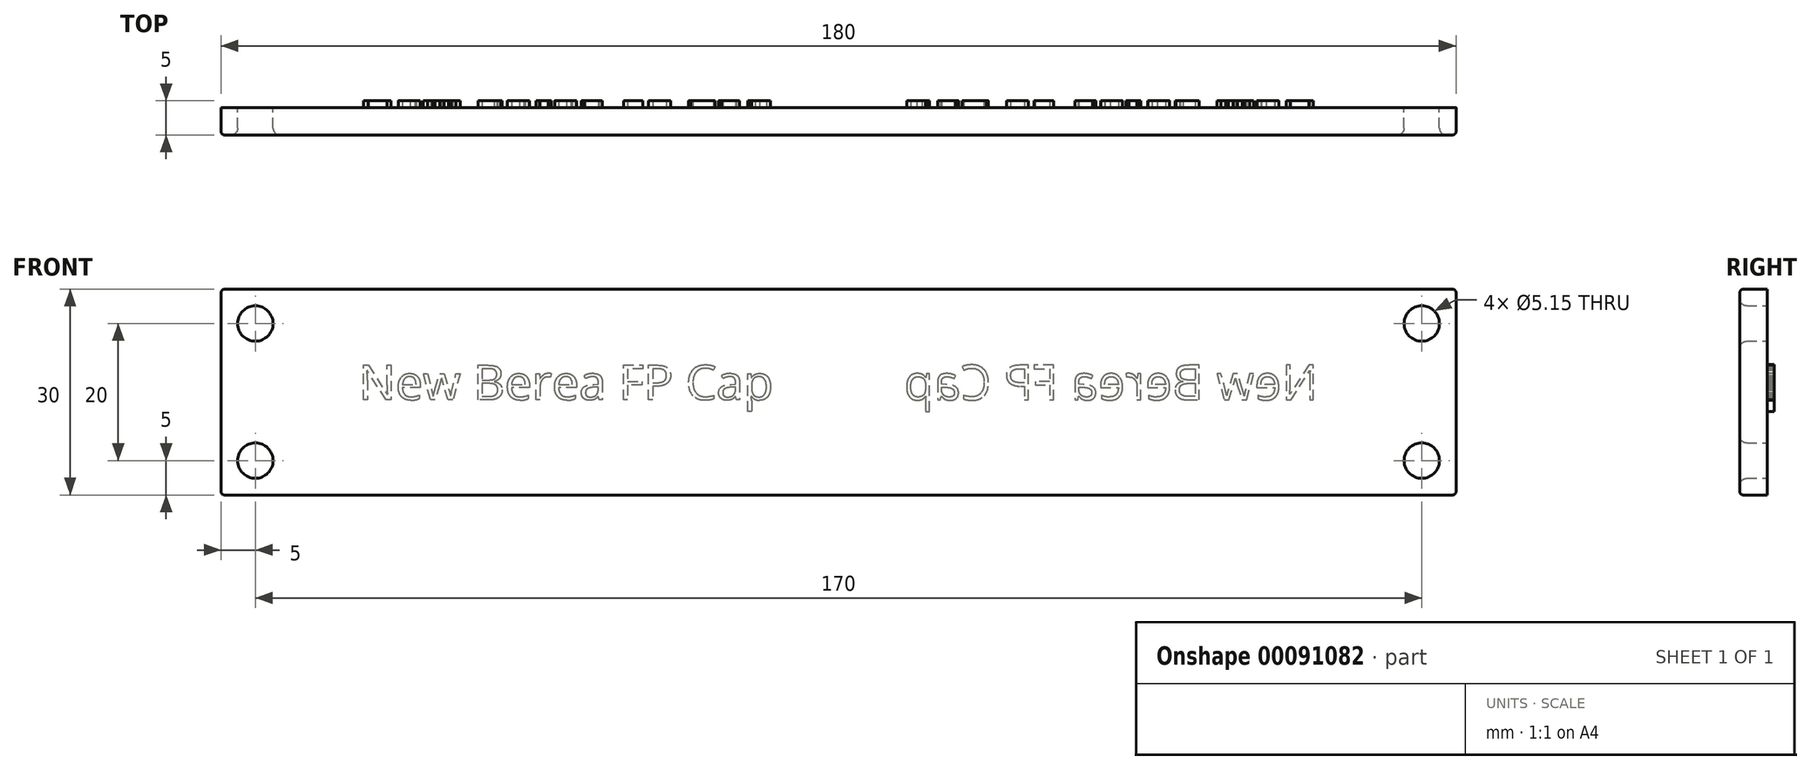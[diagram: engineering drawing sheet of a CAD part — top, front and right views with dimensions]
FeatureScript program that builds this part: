
annotation { "Feature Type Name" : "Feature", "Feature Type Description" : "" }
export const myFeature = defineFeature(function(context is Context, id is Id, definition is map)
    precondition{}
    {
        {
            var Q0;
            Q0=qCreatedBy(makeId("Front.planeOp"),FACE);
            var sketch = newSketch(context, id + "F0", { "sketchPlane" : qUnion([Q0])});
            skLineSegment(sketch, "E0.bottom", {"start": v(-90, -15) * mm, "end": v(90, -15) * mm});
            skLineSegment(sketch, "E0.top", {"start": v(-90, 15) * mm, "end": v(90, 15) * mm});
            skLineSegment(sketch, "E0.left", {"start": v(-90, -15) * mm, "end": v(-90, 15) * mm});
            skLineSegment(sketch, "E0.right", {"start": v(90, -15) * mm, "end": v(90, 15) * mm});
            skPoint(sketch, "E0.middle", {"position": v(0, 0) * mm});
            skCircle(sketch, "E1", {"center": v(-85, 10) * mm, "radius": 2.58 * mm});
            skPoint(sketch, "E2.start.orphan", {"position": v(-90, 0) * mm});
            skPoint(sketch, "E3.orphan", {"position": v(0, 15) * mm});
            skPoint(sketch, "E4.end.orphan", {"position": v(0, -15) * mm});
            skLineSegment(sketch, "E5", {"start": v(-90, 0) * mm, "end": v(0, 0) * mm, "construction": true});
            skLineSegment(sketch, "E6", {"start": v(0, 15) * mm, "end": v(0, -15) * mm, "construction": true});
            skCircle(sketch, "E7.MirrorC", {"center": v(-85, -10) * mm, "radius": 2.58 * mm});
            skCircle(sketch, "E8.MirrorC", {"center": v(85, 10) * mm, "radius": 2.58 * mm});
            skCircle(sketch, "E9.MirrorC", {"center": v(85, -10) * mm, "radius": 2.58 * mm});
            skSolve(sketch);
        }
        {
            var Q0;
            Q0=makeQuery(id+"F0.imprint","IMPRINT",FACE,{"disambiguationData":[TD([[makeQuery(id+"F0.imprint","IMPRINT",EDGE,{"derivedFrom":sQuery(id+"F0.wireOp",EDGE,"E0.bottom")}),1.0]])]});
            extrude(context, id + "F1", {"entities" : qUnion([Q0]), "depth" : 4 * mm});
        }
        {
            var Q0;
            Q0=makeQuery(id+"F1.opExtrude","CAP_EDGE",EDGE,{"disambiguationData":[OSD([sQuery(id+"F0.wireOp",EDGE,"E1")])],"isStart":false});
            var Q1;
            Q1=makeQuery(id+"F1.opExtrude","CAP_EDGE",EDGE,{"disambiguationData":[OSD([sQuery(id+"F0.wireOp",EDGE,"f5b72a5b-8583-449a-bdbf-9ac5a681e1fd0.MirrorC")])],"isStart":false});
            var Q2;
            Q2=makeQuery(id+"F1.opExtrude","CAP_EDGE",EDGE,{"disambiguationData":[OSD([sQuery(id+"F0.wireOp",EDGE,"2623e306-60f4-4522-aa65-1e3e8c2cf5b60.MirrorC")])],"isStart":false});
            var Q3;
            Q3=makeQuery(id+"F1.opExtrude","CAP_EDGE",EDGE,{"disambiguationData":[OSD([sQuery(id+"F0.wireOp",EDGE,"be81a34d-1d50-4ce7-a7a8-4484a1701fac0.MirrorC")])],"isStart":false});
            var Q4;
            Q4=makeQuery(id+"F1.opExtrude","CAP_EDGE",EDGE,{"disambiguationData":[OSD([sQuery(id+"F0.wireOp",EDGE,"E7.MirrorC")])],"isStart":false});
            var Q5;
            Q5=makeQuery(id+"F1.opExtrude","CAP_EDGE",EDGE,{"disambiguationData":[OSD([sQuery(id+"F0.wireOp",EDGE,"E8.MirrorC")])],"isStart":false});
            var Q6;
            Q6=makeQuery(id+"F1.opExtrude","CAP_EDGE",EDGE,{"disambiguationData":[OSD([sQuery(id+"F0.wireOp",EDGE,"E9.MirrorC")])],"isStart":false});
            fillet(context, id + "F2", {"entities" : qUnion([Q0, Q1, Q2, Q3, Q4, Q5, Q6]), "radius" : 1 * mm, "tangentPropagation" : true, "allowEdgeOverflow" : false});
        }
        {
            var Q0;
            Q0=makeQuery(id+"F1.opExtrude","CAP_EDGE",EDGE,{"disambiguationData":[OSD([sQuery(id+"F0.wireOp",EDGE,"E0.top")])],"isStart":false});
            var Q1;
            Q1=makeQuery(id+"F1.opExtrude","CAP_EDGE",EDGE,{"disambiguationData":[OSD([sQuery(id+"F0.wireOp",EDGE,"E0.left")])],"isStart":false});
            var Q2;
            Q2=makeQuery(id+"F1.opExtrude","CAP_EDGE",EDGE,{"disambiguationData":[OSD([sQuery(id+"F0.wireOp",EDGE,"E0.bottom")])],"isStart":false});
            var Q3;
            Q3=makeQuery(id+"F1.opExtrude","CAP_EDGE",EDGE,{"disambiguationData":[OSD([sQuery(id+"F0.wireOp",EDGE,"E0.right")])],"isStart":false});
            var Q4;
            Q4=makeQuery(id+"F1.opExtrude","SWEPT_EDGE",EDGE,{"disambiguationData":[OSD([sQuery(id+"F0.wireOp",EDGE,"E0.top"),sQuery(id+"F0.wireOp",EDGE,"E0.left")])]});
            var Q5;
            Q5=makeQuery(id+"F1.opExtrude","SWEPT_EDGE",EDGE,{"disambiguationData":[OSD([sQuery(id+"F0.wireOp",EDGE,"E0.bottom"),sQuery(id+"F0.wireOp",EDGE,"E0.left")])]});
            var Q6;
            Q6=makeQuery(id+"F1.opExtrude","SWEPT_EDGE",EDGE,{"disambiguationData":[OSD([sQuery(id+"F0.wireOp",EDGE,"E0.top"),sQuery(id+"F0.wireOp",EDGE,"E0.right")])]});
            var Q7;
            Q7=makeQuery(id+"F1.opExtrude","SWEPT_EDGE",EDGE,{"disambiguationData":[OSD([sQuery(id+"F0.wireOp",EDGE,"E0.bottom"),sQuery(id+"F0.wireOp",EDGE,"E0.right")])]});
            fillet(context, id + "F3", {"entities" : qUnion([Q0, Q1, Q2, Q3, Q4, Q5, Q6, Q7]), "radius" : .5 * mm, "tangentPropagation" : true, "allowEdgeOverflow" : false});
        }
        {
            var Q0;
            Q0=makeQuery(id+"F1.opExtrude","CAP_FACE",FACE,{"disambiguationData":[OSD([sQuery(id+"F0.wireOp",EDGE,"E0.bottom"),sQuery(id+"F0.wireOp",EDGE,"E0.top"),sQuery(id+"F0.wireOp",EDGE,"E0.left"),sQuery(id+"F0.wireOp",EDGE,"E0.right"),sQuery(id+"F0.wireOp",EDGE,"E1"),sQuery(id+"F0.wireOp",EDGE,"E7.MirrorC"),sQuery(id+"F0.wireOp",EDGE,"E8.MirrorC"),sQuery(id+"F0.wireOp",EDGE,"E9.MirrorC")])],"isStart":true});
            var sketch = newSketch(context, id + "F4", { "sketchPlane" : qUnion([Q0])});
            skText(sketch, "E10", { "text": "New Berea FP Cap", "fontName": "OpenSans-Regular.ttf"});
            skLineSegment(sketch, "E11", {"start": v(0, 15) * mm, "end": v(0, -15) * mm, "construction": true});
            const initialGuessF4  = {"E10": [-0.06991, -0.00113, 1, 0, 0.0051]};
            skSetInitialGuess(sketch, initialGuessF4);
            skSolve(sketch);
        }
        {
            var Q0;
            Q0=qSketchRegion(id+"F4",true);
            extrude(context, id + "F5", {"entities" : qUnion([Q0]), "operationType" : NewBodyOperationType.ADD, "depth" : 1 * mm});
        }
        {
            var Q0;
            Q0=makeQuery(id+"F1.opExtrude","SWEPT_BODY",BODY,{"disambiguationData":[OSD([sQuery(id+"F0.wireOp",EDGE,"E0.bottom"),sQuery(id+"F0.wireOp",EDGE,"E0.top"),sQuery(id+"F0.wireOp",EDGE,"E0.left"),sQuery(id+"F0.wireOp",EDGE,"E0.right"),sQuery(id+"F0.wireOp",EDGE,"E1"),sQuery(id+"F0.wireOp",EDGE,"E7.MirrorC"),sQuery(id+"F0.wireOp",EDGE,"E8.MirrorC"),sQuery(id+"F0.wireOp",EDGE,"E9.MirrorC")])]});
            var Q1;
            Q1=makeQuery(id+"F5.opExtrude","SWEPT_FACE",FACE,{"disambiguationData":[OSD([sQuery(id+"F4.wireOp",EDGE,"E10.sketch_text.stroke-94")])]});
            var Q2;
            Q2=makeQuery(id+"F5.opExtrude","SWEPT_FACE",FACE,{"disambiguationData":[OSD([sQuery(id+"F4.wireOp",EDGE,"E10.sketch_text.stroke-169")])]});
            var Q3;
            Q3=makeQuery(id+"F5.opExtrude","SWEPT_FACE",FACE,{"disambiguationData":[OSD([sQuery(id+"F4.wireOp",EDGE,"E10.sketch_text.stroke-185")])]});
            var Q4;
            Q4=makeQuery(id+"F5.opExtrude","SWEPT_FACE",FACE,{"disambiguationData":[OSD([sQuery(id+"F4.wireOp",EDGE,"E10.sketch_text.stroke-125")])]});
            var Q5;
            Q5=makeQuery(id+"F5.opExtrude","SWEPT_FACE",FACE,{"disambiguationData":[OSD([sQuery(id+"F4.wireOp",EDGE,"E10.sketch_text.stroke-155")])]});
            var Q6;
            Q6=makeQuery(id+"F5.opExtrude","SWEPT_FACE",FACE,{"disambiguationData":[OSD([sQuery(id+"F4.wireOp",EDGE,"E10.sketch_text.stroke-65")])]});
            var Q7;
            Q7=makeQuery(id+"F5.opExtrude","SWEPT_FACE",FACE,{"disambiguationData":[OSD([sQuery(id+"F4.wireOp",EDGE,"E10.sketch_text.stroke-81")])]});
            var Q8;
            Q8=makeQuery(id+"F5.opExtrude","SWEPT_FACE",FACE,{"disambiguationData":[OSD([sQuery(id+"F4.wireOp",EDGE,"E10.sketch_text.stroke-67")])]});
            var Q9;
            Q9=makeQuery(id+"F5.opExtrude","SWEPT_FACE",FACE,{"disambiguationData":[OSD([sQuery(id+"F4.wireOp",EDGE,"E10.sketch_text.stroke-99")])]});
            var Q10;
            Q10=makeQuery(id+"F5.opExtrude","SWEPT_FACE",FACE,{"disambiguationData":[OSD([sQuery(id+"F4.wireOp",EDGE,"E10.sketch_text.stroke-127")])]});
            var Q11;
            Q11=makeQuery(id+"F5.opExtrude","SWEPT_FACE",FACE,{"disambiguationData":[OSD([sQuery(id+"F4.wireOp",EDGE,"E10.sketch_text.stroke-10")])]});
            var Q12;
            Q12=makeQuery(id+"F5.opExtrude","CAP_FACE",FACE,{"disambiguationData":[OSD([sQuery(id+"F4.wireOp",EDGE,"E10.sketch_text.stroke-9"),sQuery(id+"F4.wireOp",EDGE,"E10.sketch_text.stroke-10"),sQuery(id+"F4.wireOp",EDGE,"E10.sketch_text.stroke-11"),sQuery(id+"F4.wireOp",EDGE,"E10.sketch_text.stroke-12")])],"isStart":false});
            var Q13;
            Q13=makeQuery(id+"F5.opExtrude","SWEPT_FACE",FACE,{"disambiguationData":[OSD([sQuery(id+"F4.wireOp",EDGE,"E10.sketch_text.stroke-154")])]});
            var Q14;
            Q14=makeQuery(id+"F5.opExtrude","SWEPT_FACE",FACE,{"disambiguationData":[OSD([sQuery(id+"F4.wireOp",EDGE,"E10.sketch_text.stroke-1")])]});
            var Q15;
            Q15=makeQuery(id+"F5.opExtrude","CAP_FACE",FACE,{"disambiguationData":[OSD([sQuery(id+"F4.wireOp",EDGE,"E10.sketch_text.stroke-124"),sQuery(id+"F4.wireOp",EDGE,"E10.sketch_text.stroke-125"),sQuery(id+"F4.wireOp",EDGE,"E10.sketch_text.stroke-126"),sQuery(id+"F4.wireOp",EDGE,"E10.sketch_text.stroke-127"),sQuery(id+"F4.wireOp",EDGE,"E10.sketch_text.stroke-128"),sQuery(id+"F4.wireOp",EDGE,"E10.sketch_text.stroke-129"),sQuery(id+"F4.wireOp",EDGE,"E10.sketch_text.stroke-130"),sQuery(id+"F4.wireOp",EDGE,"E10.sketch_text.stroke-131"),sQuery(id+"F4.wireOp",EDGE,"E10.sketch_text.stroke-132"),sQuery(id+"F4.wireOp",EDGE,"E10.sketch_text.stroke-133"),sQuery(id+"F4.wireOp",EDGE,"E10.sketch_text.stroke-134"),sQuery(id+"F4.wireOp",EDGE,"E10.sketch_text.stroke-135"),sQuery(id+"F4.wireOp",EDGE,"E10.sketch_text.stroke-136"),sQuery(id+"F4.wireOp",EDGE,"E10.sketch_text.stroke-137"),sQuery(id+"F4.wireOp",EDGE,"E10.sketch_text.stroke-138")])],"isStart":false});
            var Q16;
            Q16=makeQuery(id+"F5.opExtrude","CAP_FACE",FACE,{"disambiguationData":[OSD([sQuery(id+"F4.wireOp",EDGE,"E10.sketch_text.stroke-34"),sQuery(id+"F4.wireOp",EDGE,"E10.sketch_text.stroke-35"),sQuery(id+"F4.wireOp",EDGE,"E10.sketch_text.stroke-36"),sQuery(id+"F4.wireOp",EDGE,"E10.sketch_text.stroke-37"),sQuery(id+"F4.wireOp",EDGE,"E10.sketch_text.stroke-38"),sQuery(id+"F4.wireOp",EDGE,"E10.sketch_text.stroke-39"),sQuery(id+"F4.wireOp",EDGE,"E10.sketch_text.stroke-40"),sQuery(id+"F4.wireOp",EDGE,"E10.sketch_text.stroke-41"),sQuery(id+"F4.wireOp",EDGE,"E10.sketch_text.stroke-42"),sQuery(id+"F4.wireOp",EDGE,"E10.sketch_text.stroke-43"),sQuery(id+"F4.wireOp",EDGE,"E10.sketch_text.stroke-44"),sQuery(id+"F4.wireOp",EDGE,"E10.sketch_text.stroke-45"),sQuery(id+"F4.wireOp",EDGE,"E10.sketch_text.stroke-46"),sQuery(id+"F4.wireOp",EDGE,"E10.sketch_text.stroke-47"),sQuery(id+"F4.wireOp",EDGE,"E10.sketch_text.stroke-48"),sQuery(id+"F4.wireOp",EDGE,"E10.sketch_text.stroke-49"),sQuery(id+"F4.wireOp",EDGE,"E10.sketch_text.stroke-50"),sQuery(id+"F4.wireOp",EDGE,"E10.sketch_text.stroke-51"),sQuery(id+"F4.wireOp",EDGE,"E10.sketch_text.stroke-52"),sQuery(id+"F4.wireOp",EDGE,"E10.sketch_text.stroke-53"),sQuery(id+"F4.wireOp",EDGE,"E10.sketch_text.stroke-54"),sQuery(id+"F4.wireOp",EDGE,"E10.sketch_text.stroke-55"),sQuery(id+"F4.wireOp",EDGE,"E10.sketch_text.stroke-56"),sQuery(id+"F4.wireOp",EDGE,"E10.sketch_text.stroke-57"),sQuery(id+"F4.wireOp",EDGE,"E10.sketch_text.stroke-58"),sQuery(id+"F4.wireOp",EDGE,"E10.sketch_text.stroke-59"),sQuery(id+"F4.wireOp",EDGE,"E10.sketch_text.stroke-60")])],"isStart":false});
            var Q17;
            Q17=makeQuery(id+"F5.opExtrude","SWEPT_FACE",FACE,{"disambiguationData":[OSD([sQuery(id+"F4.wireOp",EDGE,"E10.sketch_text.stroke-50")])]});
            var Q18;
            Q18=makeQuery(id+"F5.opExtrude","SWEPT_FACE",FACE,{"disambiguationData":[OSD([sQuery(id+"F4.wireOp",EDGE,"E10.sketch_text.stroke-2")])]});
            var Q19;
            Q19=makeQuery(id+"F5.opExtrude","SWEPT_FACE",FACE,{"disambiguationData":[OSD([sQuery(id+"F4.wireOp",EDGE,"E10.sketch_text.stroke-3")])]});
            var Q20;
            Q20=makeQuery(id+"F5.opExtrude","SWEPT_FACE",FACE,{"disambiguationData":[OSD([sQuery(id+"F4.wireOp",EDGE,"E10.sketch_text.stroke-5")])]});
            var Q21;
            Q21=makeQuery(id+"F5.opExtrude","SWEPT_FACE",FACE,{"disambiguationData":[OSD([sQuery(id+"F4.wireOp",EDGE,"E10.sketch_text.stroke-8")])]});
            var Q22;
            Q22=makeQuery(id+"F5.opExtrude","SWEPT_FACE",FACE,{"disambiguationData":[OSD([sQuery(id+"F4.wireOp",EDGE,"E10.sketch_text.stroke-98")])]});
            var Q23;
            Q23=makeQuery(id+"F5.opExtrude","SWEPT_FACE",FACE,{"disambiguationData":[OSD([sQuery(id+"F4.wireOp",EDGE,"E10.sketch_text.stroke-66")])]});
            var Q24;
            Q24=makeQuery(id+"F5.opExtrude","SWEPT_FACE",FACE,{"disambiguationData":[OSD([sQuery(id+"F4.wireOp",EDGE,"E10.sketch_text.stroke-153")])]});
            var Q25;
            Q25=makeQuery(id+"F5.opExtrude","SWEPT_FACE",FACE,{"disambiguationData":[OSD([sQuery(id+"F4.wireOp",EDGE,"E10.sketch_text.stroke-126")])]});
            var Q26;
            Q26=makeQuery(id+"F5.opExtrude","SWEPT_FACE",FACE,{"disambiguationData":[OSD([sQuery(id+"F4.wireOp",EDGE,"E10.sketch_text.stroke-183")])]});
            var Q27;
            Q27=makeQuery(id+"F5.opExtrude","SWEPT_FACE",FACE,{"disambiguationData":[OSD([sQuery(id+"F4.wireOp",EDGE,"E10.sketch_text.stroke-109")])]});
            var Q28;
            Q28=makeQuery(id+"F5.opExtrude","SWEPT_FACE",FACE,{"disambiguationData":[OSD([sQuery(id+"F4.wireOp",EDGE,"E10.sketch_text.stroke-186")])]});
            var Q29;
            Q29=makeQuery(id+"F5.opExtrude","SWEPT_FACE",FACE,{"disambiguationData":[OSD([sQuery(id+"F4.wireOp",EDGE,"E10.sketch_text.stroke-79")])]});
            var Q30;
            Q30=makeQuery(id+"F5.opExtrude","SWEPT_FACE",FACE,{"disambiguationData":[OSD([sQuery(id+"F4.wireOp",EDGE,"E10.sketch_text.stroke-110")])]});
            var Q31;
            Q31=makeQuery(id+"F5.opExtrude","SWEPT_FACE",FACE,{"disambiguationData":[OSD([sQuery(id+"F4.wireOp",EDGE,"E10.sketch_text.stroke-38")])]});
            var Q32;
            Q32=makeQuery(id+"F5.opExtrude","SWEPT_FACE",FACE,{"disambiguationData":[OSD([sQuery(id+"F4.wireOp",EDGE,"E10.sketch_text.stroke-24")])]});
            var Q33;
            Q33=makeQuery(id+"F5.opExtrude","SWEPT_FACE",FACE,{"disambiguationData":[OSD([sQuery(id+"F4.wireOp",EDGE,"E10.sketch_text.stroke-12")])]});
            var Q34;
            Q34=makeQuery(id+"F5.opExtrude","SWEPT_FACE",FACE,{"disambiguationData":[OSD([sQuery(id+"F4.wireOp",EDGE,"E10.sketch_text.stroke-100")])]});
            var Q35;
            Q35=makeQuery(id+"F5.opExtrude","SWEPT_FACE",FACE,{"disambiguationData":[OSD([sQuery(id+"F4.wireOp",EDGE,"E10.sketch_text.stroke-158")])]});
            var Q36;
            Q36=makeQuery(id+"F5.opExtrude","SWEPT_FACE",FACE,{"disambiguationData":[OSD([sQuery(id+"F4.wireOp",EDGE,"E10.sketch_text.stroke-142")])]});
            var Q37;
            Q37=makeQuery(id+"F5.opExtrude","SWEPT_FACE",FACE,{"disambiguationData":[OSD([sQuery(id+"F4.wireOp",EDGE,"E10.sketch_text.stroke-54")])]});
            var Q38;
            Q38=makeQuery(id+"F5.opExtrude","SWEPT_FACE",FACE,{"disambiguationData":[OSD([sQuery(id+"F4.wireOp",EDGE,"E10.sketch_text.stroke-25")])]});
            var Q39;
            Q39=makeQuery(id+"F5.opExtrude","SWEPT_FACE",FACE,{"disambiguationData":[OSD([sQuery(id+"F4.wireOp",EDGE,"E10.sketch_text.stroke-101")])]});
            var Q40;
            Q40=makeQuery(id+"F5.opExtrude","SWEPT_FACE",FACE,{"disambiguationData":[OSD([sQuery(id+"F4.wireOp",EDGE,"E10.sketch_text.stroke-69")])]});
            var Q41;
            Q41=makeQuery(id+"F5.opExtrude","SWEPT_FACE",FACE,{"disambiguationData":[OSD([sQuery(id+"F4.wireOp",EDGE,"E10.sketch_text.stroke-159")])]});
            var Q42;
            Q42=makeQuery(id+"F5.opExtrude","SWEPT_FACE",FACE,{"disambiguationData":[OSD([sQuery(id+"F4.wireOp",EDGE,"E10.sketch_text.stroke-85")])]});
            var Q43;
            Q43=makeQuery(id+"F5.opExtrude","SWEPT_FACE",FACE,{"disambiguationData":[OSD([sQuery(id+"F4.wireOp",EDGE,"E10.sketch_text.stroke-173")])]});
            var Q44;
            Q44=makeQuery(id+"F5.opExtrude","SWEPT_FACE",FACE,{"disambiguationData":[OSD([sQuery(id+"F4.wireOp",EDGE,"E10.sketch_text.stroke-40")])]});
            var Q45;
            Q45=makeQuery(id+"F5.opExtrude","SWEPT_FACE",FACE,{"disambiguationData":[OSD([sQuery(id+"F4.wireOp",EDGE,"E10.sketch_text.stroke-102")])]});
            var Q46;
            Q46=makeQuery(id+"F5.opExtrude","SWEPT_FACE",FACE,{"disambiguationData":[OSD([sQuery(id+"F4.wireOp",EDGE,"E10.sketch_text.stroke-86")])]});
            var Q47;
            Q47=makeQuery(id+"F5.opExtrude","SWEPT_FACE",FACE,{"disambiguationData":[OSD([sQuery(id+"F4.wireOp",EDGE,"E10.sketch_text.stroke-130")])]});
            var Q48;
            Q48=makeQuery(id+"F5.opExtrude","SWEPT_FACE",FACE,{"disambiguationData":[OSD([sQuery(id+"F4.wireOp",EDGE,"E10.sketch_text.stroke-103")])]});
            var Q49;
            Q49=makeQuery(id+"F5.opExtrude","SWEPT_FACE",FACE,{"disambiguationData":[OSD([sQuery(id+"F4.wireOp",EDGE,"E10.sketch_text.stroke-87")])]});
            var Q50;
            Q50=makeQuery(id+"F5.opExtrude","SWEPT_FACE",FACE,{"disambiguationData":[OSD([sQuery(id+"F4.wireOp",EDGE,"E10.sketch_text.stroke-145")])]});
            var Q51;
            Q51=makeQuery(id+"F5.opExtrude","SWEPT_FACE",FACE,{"disambiguationData":[OSD([sQuery(id+"F4.wireOp",EDGE,"E10.sketch_text.stroke-131")])]});
            var Q52;
            Q52=makeQuery(id+"F5.opExtrude","SWEPT_FACE",FACE,{"disambiguationData":[OSD([sQuery(id+"F4.wireOp",EDGE,"E10.sketch_text.stroke-28")])]});
            var Q53;
            Q53=makeQuery(id+"F5.opExtrude","SWEPT_FACE",FACE,{"disambiguationData":[OSD([sQuery(id+"F4.wireOp",EDGE,"E10.sketch_text.stroke-14")])]});
            var Q54;
            Q54=makeQuery(id+"F5.opExtrude","SWEPT_FACE",FACE,{"disambiguationData":[OSD([sQuery(id+"F4.wireOp",EDGE,"E10.sketch_text.stroke-88")])]});
            var Q55;
            Q55=makeQuery(id+"F5.opExtrude","SWEPT_FACE",FACE,{"disambiguationData":[OSD([sQuery(id+"F4.wireOp",EDGE,"E10.sketch_text.stroke-162")])]});
            var Q56;
            Q56=makeQuery(id+"F5.opExtrude","SWEPT_FACE",FACE,{"disambiguationData":[OSD([sQuery(id+"F4.wireOp",EDGE,"E10.sketch_text.stroke-176")])]});
            var Q57;
            Q57=makeQuery(id+"F5.opExtrude","SWEPT_FACE",FACE,{"disambiguationData":[OSD([sQuery(id+"F4.wireOp",EDGE,"E10.sketch_text.stroke-73")])]});
            var Q58;
            Q58=makeQuery(id+"F5.opExtrude","SWEPT_FACE",FACE,{"disambiguationData":[OSD([sQuery(id+"F4.wireOp",EDGE,"E10.sketch_text.stroke-59")])]});
            var Q59;
            Q59=makeQuery(id+"F5.opExtrude","SWEPT_FACE",FACE,{"disambiguationData":[OSD([sQuery(id+"F4.wireOp",EDGE,"E10.sketch_text.stroke-133")])]});
            var Q60;
            Q60=makeQuery(id+"F5.opExtrude","SWEPT_FACE",FACE,{"disambiguationData":[OSD([sQuery(id+"F4.wireOp",EDGE,"E10.sketch_text.stroke-119")])]});
            var Q61;
            Q61=makeQuery(id+"F5.opExtrude","SWEPT_FACE",FACE,{"disambiguationData":[OSD([sQuery(id+"F4.wireOp",EDGE,"E10.sketch_text.stroke-74")])]});
            var Q62;
            Q62=makeQuery(id+"F5.opExtrude","SWEPT_FACE",FACE,{"disambiguationData":[OSD([sQuery(id+"F4.wireOp",EDGE,"E10.sketch_text.stroke-44")])]});
            var Q63;
            Q63=makeQuery(id+"F5.opExtrude","SWEPT_FACE",FACE,{"disambiguationData":[OSD([sQuery(id+"F4.wireOp",EDGE,"E10.sketch_text.stroke-120")])]});
            var Q64;
            Q64=makeQuery(id+"F5.opExtrude","SWEPT_FACE",FACE,{"disambiguationData":[OSD([sQuery(id+"F4.wireOp",EDGE,"E10.sketch_text.stroke-90")])]});
            var Q65;
            Q65=makeQuery(id+"F5.opExtrude","SWEPT_FACE",FACE,{"disambiguationData":[OSD([sQuery(id+"F4.wireOp",EDGE,"E10.sketch_text.stroke-178")])]});
            var Q66;
            Q66=makeQuery(id+"F5.opExtrude","SWEPT_FACE",FACE,{"disambiguationData":[OSD([sQuery(id+"F4.wireOp",EDGE,"E10.sketch_text.stroke-45")])]});
            var Q67;
            Q67=makeQuery(id+"F5.opExtrude","SWEPT_FACE",FACE,{"disambiguationData":[OSD([sQuery(id+"F4.wireOp",EDGE,"E10.sketch_text.stroke-31")])]});
            var Q68;
            Q68=makeQuery(id+"F5.opExtrude","SWEPT_FACE",FACE,{"disambiguationData":[OSD([sQuery(id+"F4.wireOp",EDGE,"E10.sketch_text.stroke-135")])]});
            var Q69;
            Q69=makeQuery(id+"F5.opExtrude","SWEPT_FACE",FACE,{"disambiguationData":[OSD([sQuery(id+"F4.wireOp",EDGE,"E10.sketch_text.stroke-179")])]});
            var Q70;
            Q70=makeQuery(id+"F5.opExtrude","SWEPT_FACE",FACE,{"disambiguationData":[OSD([sQuery(id+"F4.wireOp",EDGE,"E10.sketch_text.stroke-165")])]});
            var Q71;
            Q71=makeQuery(id+"F5.opExtrude","SWEPT_FACE",FACE,{"disambiguationData":[OSD([sQuery(id+"F4.wireOp",EDGE,"E10.sketch_text.stroke-149")])]});
            var Q72;
            Q72=makeQuery(id+"F5.opExtrude","SWEPT_FACE",FACE,{"disambiguationData":[OSD([sQuery(id+"F4.wireOp",EDGE,"E10.sketch_text.stroke-136")])]});
            var Q73;
            Q73=makeQuery(id+"F5.opExtrude","SWEPT_FACE",FACE,{"disambiguationData":[OSD([sQuery(id+"F4.wireOp",EDGE,"E10.sketch_text.stroke-122")])]});
            var Q74;
            Q74=makeQuery(id+"F5.opExtrude","SWEPT_FACE",FACE,{"disambiguationData":[OSD([sQuery(id+"F4.wireOp",EDGE,"E10.sketch_text.stroke-106")])]});
            var Q75;
            Q75=makeQuery(id+"F5.opExtrude","SWEPT_FACE",FACE,{"disambiguationData":[OSD([sQuery(id+"F4.wireOp",EDGE,"E10.sketch_text.stroke-180")])]});
            var Q76;
            Q76=makeQuery(id+"F5.opExtrude","SWEPT_FACE",FACE,{"disambiguationData":[OSD([sQuery(id+"F4.wireOp",EDGE,"E10.sketch_text.stroke-166")])]});
            var Q77;
            Q77=makeQuery(id+"F5.opExtrude","SWEPT_FACE",FACE,{"disambiguationData":[OSD([sQuery(id+"F4.wireOp",EDGE,"E10.sketch_text.stroke-150")])]});
            var Q78;
            Q78=makeQuery(id+"F5.opExtrude","SWEPT_FACE",FACE,{"disambiguationData":[OSD([sQuery(id+"F4.wireOp",EDGE,"E10.sketch_text.stroke-76")])]});
            var Q79;
            Q79=makeQuery(id+"F5.opExtrude","SWEPT_FACE",FACE,{"disambiguationData":[OSD([sQuery(id+"F4.wireOp",EDGE,"E10.sketch_text.stroke-32")])]});
            var Q80;
            Q80=makeQuery(id+"F5.opExtrude","SWEPT_FACE",FACE,{"disambiguationData":[OSD([sQuery(id+"F4.wireOp",EDGE,"E10.sketch_text.stroke-181")])]});
            var Q81;
            Q81=makeQuery(id+"F5.opExtrude","SWEPT_FACE",FACE,{"disambiguationData":[OSD([sQuery(id+"F4.wireOp",EDGE,"E10.sketch_text.stroke-47")])]});
            var Q82;
            Q82=makeQuery(id+"F5.opExtrude","SWEPT_FACE",FACE,{"disambiguationData":[OSD([sQuery(id+"F4.wireOp",EDGE,"E10.sketch_text.stroke-123")])]});
            var Q83;
            Q83=makeQuery(id+"F5.opExtrude","SWEPT_FACE",FACE,{"disambiguationData":[OSD([sQuery(id+"F4.wireOp",EDGE,"E10.sketch_text.stroke-107")])]});
            var Q84;
            Q84=makeQuery(id+"F5.opExtrude","SWEPT_FACE",FACE,{"disambiguationData":[OSD([sQuery(id+"F4.wireOp",EDGE,"E10.sketch_text.stroke-48")])]});
            var Q85;
            Q85=makeQuery(id+"F5.opExtrude","SWEPT_FACE",FACE,{"disambiguationData":[OSD([sQuery(id+"F4.wireOp",EDGE,"E10.sketch_text.stroke-124")])]});
            var Q86;
            Q86=makeQuery(id+"F5.opExtrude","SWEPT_FACE",FACE,{"disambiguationData":[OSD([sQuery(id+"F4.wireOp",EDGE,"E10.sketch_text.stroke-108")])]});
            var Q87;
            Q87=makeQuery(id+"F5.opExtrude","CAP_FACE",FACE,{"disambiguationData":[OSD([sQuery(id+"F4.wireOp",EDGE,"E10.sketch_text.stroke-139"),sQuery(id+"F4.wireOp",EDGE,"E10.sketch_text.stroke-140"),sQuery(id+"F4.wireOp",EDGE,"E10.sketch_text.stroke-141"),sQuery(id+"F4.wireOp",EDGE,"E10.sketch_text.stroke-142"),sQuery(id+"F4.wireOp",EDGE,"E10.sketch_text.stroke-143"),sQuery(id+"F4.wireOp",EDGE,"E10.sketch_text.stroke-144"),sQuery(id+"F4.wireOp",EDGE,"E10.sketch_text.stroke-145"),sQuery(id+"F4.wireOp",EDGE,"E10.sketch_text.stroke-146"),sQuery(id+"F4.wireOp",EDGE,"E10.sketch_text.stroke-147"),sQuery(id+"F4.wireOp",EDGE,"E10.sketch_text.stroke-148"),sQuery(id+"F4.wireOp",EDGE,"E10.sketch_text.stroke-149"),sQuery(id+"F4.wireOp",EDGE,"E10.sketch_text.stroke-150"),sQuery(id+"F4.wireOp",EDGE,"E10.sketch_text.stroke-151"),sQuery(id+"F4.wireOp",EDGE,"E10.sketch_text.stroke-152"),sQuery(id+"F4.wireOp",EDGE,"E10.sketch_text.stroke-153"),sQuery(id+"F4.wireOp",EDGE,"E10.sketch_text.stroke-154"),sQuery(id+"F4.wireOp",EDGE,"E10.sketch_text.stroke-155"),sQuery(id+"F4.wireOp",EDGE,"E10.sketch_text.stroke-156"),sQuery(id+"F4.wireOp",EDGE,"E10.sketch_text.stroke-157"),sQuery(id+"F4.wireOp",EDGE,"E10.sketch_text.stroke-158"),sQuery(id+"F4.wireOp",EDGE,"E10.sketch_text.stroke-159"),sQuery(id+"F4.wireOp",EDGE,"E10.sketch_text.stroke-160"),sQuery(id+"F4.wireOp",EDGE,"E10.sketch_text.stroke-161"),sQuery(id+"F4.wireOp",EDGE,"E10.sketch_text.stroke-162"),sQuery(id+"F4.wireOp",EDGE,"E10.sketch_text.stroke-163"),sQuery(id+"F4.wireOp",EDGE,"E10.sketch_text.stroke-164"),sQuery(id+"F4.wireOp",EDGE,"E10.sketch_text.stroke-165")])],"isStart":false});
            var Q88;
            Q88=makeQuery(id+"F5.opExtrude","CAP_FACE",FACE,{"disambiguationData":[OSD([sQuery(id+"F4.wireOp",EDGE,"E10.sketch_text.stroke-21"),sQuery(id+"F4.wireOp",EDGE,"E10.sketch_text.stroke-22"),sQuery(id+"F4.wireOp",EDGE,"E10.sketch_text.stroke-23"),sQuery(id+"F4.wireOp",EDGE,"E10.sketch_text.stroke-24"),sQuery(id+"F4.wireOp",EDGE,"E10.sketch_text.stroke-25"),sQuery(id+"F4.wireOp",EDGE,"E10.sketch_text.stroke-26"),sQuery(id+"F4.wireOp",EDGE,"E10.sketch_text.stroke-27"),sQuery(id+"F4.wireOp",EDGE,"E10.sketch_text.stroke-28"),sQuery(id+"F4.wireOp",EDGE,"E10.sketch_text.stroke-29"),sQuery(id+"F4.wireOp",EDGE,"E10.sketch_text.stroke-30"),sQuery(id+"F4.wireOp",EDGE,"E10.sketch_text.stroke-31"),sQuery(id+"F4.wireOp",EDGE,"E10.sketch_text.stroke-32"),sQuery(id+"F4.wireOp",EDGE,"E10.sketch_text.stroke-33")])],"isStart":false});
            var Q89;
            Q89=makeQuery(id+"F5.opExtrude","SWEPT_FACE",FACE,{"disambiguationData":[OSD([sQuery(id+"F4.wireOp",EDGE,"E10.sketch_text.stroke-113")])]});
            var Q90;
            Q90=makeQuery(id+"F5.opExtrude","SWEPT_FACE",FACE,{"disambiguationData":[OSD([sQuery(id+"F4.wireOp",EDGE,"E10.sketch_text.stroke-37")])]});
            var Q91;
            Q91=makeQuery(id+"F5.opExtrude","SWEPT_FACE",FACE,{"disambiguationData":[OSD([sQuery(id+"F4.wireOp",EDGE,"E10.sketch_text.stroke-187")])]});
            var Q92;
            Q92=makeQuery(id+"F5.opExtrude","SWEPT_FACE",FACE,{"disambiguationData":[OSD([sQuery(id+"F4.wireOp",EDGE,"E10.sketch_text.stroke-0")])]});
            var Q93;
            Q93=makeQuery(id+"F5.opExtrude","SWEPT_FACE",FACE,{"disambiguationData":[OSD([sQuery(id+"F4.wireOp",EDGE,"E10.sketch_text.stroke-4")])]});
            var Q94;
            Q94=makeQuery(id+"F5.opExtrude","SWEPT_FACE",FACE,{"disambiguationData":[OSD([sQuery(id+"F4.wireOp",EDGE,"E10.sketch_text.stroke-82")])]});
            var Q95;
            Q95=makeQuery(id+"F5.opExtrude","SWEPT_FACE",FACE,{"disambiguationData":[OSD([sQuery(id+"F4.wireOp",EDGE,"E10.sketch_text.stroke-52")])]});
            var Q96;
            Q96=makeQuery(id+"F5.opExtrude","SWEPT_FACE",FACE,{"disambiguationData":[OSD([sQuery(id+"F4.wireOp",EDGE,"E10.sketch_text.stroke-49")])]});
            var Q97;
            Q97=makeQuery(id+"F5.opExtrude","SWEPT_FACE",FACE,{"disambiguationData":[OSD([sQuery(id+"F4.wireOp",EDGE,"E10.sketch_text.stroke-63")])]});
            var Q98;
            Q98=makeQuery(id+"F5.opExtrude","SWEPT_FACE",FACE,{"disambiguationData":[OSD([sQuery(id+"F4.wireOp",EDGE,"E10.sketch_text.stroke-21")])]});
            var Q99;
            Q99=makeQuery(id+"F5.opExtrude","SWEPT_FACE",FACE,{"disambiguationData":[OSD([sQuery(id+"F4.wireOp",EDGE,"E10.sketch_text.stroke-128")])]});
            var Q100;
            Q100=makeQuery(id+"F5.opExtrude","SWEPT_FACE",FACE,{"disambiguationData":[OSD([sQuery(id+"F4.wireOp",EDGE,"E10.sketch_text.stroke-55")])]});
            var Q101;
            Q101=makeQuery(id+"F5.opExtrude","SWEPT_FACE",FACE,{"disambiguationData":[OSD([sQuery(id+"F4.wireOp",EDGE,"E10.sketch_text.stroke-26")])]});
            var Q102;
            Q102=makeQuery(id+"F5.opExtrude","SWEPT_FACE",FACE,{"disambiguationData":[OSD([sQuery(id+"F4.wireOp",EDGE,"E10.sketch_text.stroke-174")])]});
            var Q103;
            Q103=makeQuery(id+"F5.opExtrude","SWEPT_FACE",FACE,{"disambiguationData":[OSD([sQuery(id+"F4.wireOp",EDGE,"E10.sketch_text.stroke-104")])]});
            var Q104;
            Q104=makeQuery(id+"F5.opExtrude","SWEPT_FACE",FACE,{"disambiguationData":[OSD([sQuery(id+"F4.wireOp",EDGE,"E10.sketch_text.stroke-72")])]});
            var Q105;
            Q105=makeQuery(id+"F5.opExtrude","SWEPT_FACE",FACE,{"disambiguationData":[OSD([sQuery(id+"F4.wireOp",EDGE,"E10.sketch_text.stroke-132")])]});
            var Q106;
            Q106=makeQuery(id+"F5.opExtrude","SWEPT_FACE",FACE,{"disambiguationData":[OSD([sQuery(id+"F4.wireOp",EDGE,"E10.sketch_text.stroke-43")])]});
            var Q107;
            Q107=makeQuery(id+"F5.opExtrude","SWEPT_FACE",FACE,{"disambiguationData":[OSD([sQuery(id+"F4.wireOp",EDGE,"E10.sketch_text.stroke-15")])]});
            var Q108;
            Q108=makeQuery(id+"F5.opExtrude","SWEPT_FACE",FACE,{"disambiguationData":[OSD([sQuery(id+"F4.wireOp",EDGE,"E10.sketch_text.stroke-89")])]});
            var Q109;
            Q109=makeQuery(id+"F5.opExtrude","SWEPT_FACE",FACE,{"disambiguationData":[OSD([sQuery(id+"F4.wireOp",EDGE,"E10.sketch_text.stroke-163")])]});
            var Q110;
            Q110=makeQuery(id+"F5.opExtrude","SWEPT_FACE",FACE,{"disambiguationData":[OSD([sQuery(id+"F4.wireOp",EDGE,"E10.sketch_text.stroke-30")])]});
            var Q111;
            Q111=makeQuery(id+"F5.opExtrude","SWEPT_FACE",FACE,{"disambiguationData":[OSD([sQuery(id+"F4.wireOp",EDGE,"E10.sketch_text.stroke-134")])]});
            var Q112;
            Q112=makeQuery(id+"F5.opExtrude","SWEPT_FACE",FACE,{"disambiguationData":[OSD([sQuery(id+"F4.wireOp",EDGE,"E10.sketch_text.stroke-121")])]});
            var Q113;
            Q113=makeQuery(id+"F5.opExtrude","CAP_FACE",FACE,{"disambiguationData":[OSD([sQuery(id+"F4.wireOp",EDGE,"E10.sketch_text.stroke-105"),sQuery(id+"F4.wireOp",EDGE,"E10.sketch_text.stroke-106"),sQuery(id+"F4.wireOp",EDGE,"E10.sketch_text.stroke-107"),sQuery(id+"F4.wireOp",EDGE,"E10.sketch_text.stroke-108"),sQuery(id+"F4.wireOp",EDGE,"E10.sketch_text.stroke-109"),sQuery(id+"F4.wireOp",EDGE,"E10.sketch_text.stroke-110"),sQuery(id+"F4.wireOp",EDGE,"E10.sketch_text.stroke-111"),sQuery(id+"F4.wireOp",EDGE,"E10.sketch_text.stroke-112"),sQuery(id+"F4.wireOp",EDGE,"E10.sketch_text.stroke-113"),sQuery(id+"F4.wireOp",EDGE,"E10.sketch_text.stroke-114"),sQuery(id+"F4.wireOp",EDGE,"E10.sketch_text.stroke-115"),sQuery(id+"F4.wireOp",EDGE,"E10.sketch_text.stroke-116"),sQuery(id+"F4.wireOp",EDGE,"E10.sketch_text.stroke-117"),sQuery(id+"F4.wireOp",EDGE,"E10.sketch_text.stroke-118"),sQuery(id+"F4.wireOp",EDGE,"E10.sketch_text.stroke-119"),sQuery(id+"F4.wireOp",EDGE,"E10.sketch_text.stroke-120"),sQuery(id+"F4.wireOp",EDGE,"E10.sketch_text.stroke-121"),sQuery(id+"F4.wireOp",EDGE,"E10.sketch_text.stroke-122"),sQuery(id+"F4.wireOp",EDGE,"E10.sketch_text.stroke-123")])],"isStart":false});
            var Q114;
            Q114=makeQuery(id+"F5.opExtrude","SWEPT_FACE",FACE,{"disambiguationData":[OSD([sQuery(id+"F4.wireOp",EDGE,"E10.sketch_text.stroke-92")])]});
            var Q115;
            Q115=makeQuery(id+"F5.opExtrude","SWEPT_FACE",FACE,{"disambiguationData":[OSD([sQuery(id+"F4.wireOp",EDGE,"E10.sketch_text.stroke-46")])]});
            var Q116;
            Q116=makeQuery(id+"F5.opExtrude","CAP_FACE",FACE,{"disambiguationData":[OSD([sQuery(id+"F4.wireOp",EDGE,"E10.sketch_text.stroke-61"),sQuery(id+"F4.wireOp",EDGE,"E10.sketch_text.stroke-62"),sQuery(id+"F4.wireOp",EDGE,"E10.sketch_text.stroke-63"),sQuery(id+"F4.wireOp",EDGE,"E10.sketch_text.stroke-64"),sQuery(id+"F4.wireOp",EDGE,"E10.sketch_text.stroke-65"),sQuery(id+"F4.wireOp",EDGE,"E10.sketch_text.stroke-66"),sQuery(id+"F4.wireOp",EDGE,"E10.sketch_text.stroke-67"),sQuery(id+"F4.wireOp",EDGE,"E10.sketch_text.stroke-68"),sQuery(id+"F4.wireOp",EDGE,"E10.sketch_text.stroke-69"),sQuery(id+"F4.wireOp",EDGE,"E10.sketch_text.stroke-70"),sQuery(id+"F4.wireOp",EDGE,"E10.sketch_text.stroke-71"),sQuery(id+"F4.wireOp",EDGE,"E10.sketch_text.stroke-72"),sQuery(id+"F4.wireOp",EDGE,"E10.sketch_text.stroke-73"),sQuery(id+"F4.wireOp",EDGE,"E10.sketch_text.stroke-74"),sQuery(id+"F4.wireOp",EDGE,"E10.sketch_text.stroke-75"),sQuery(id+"F4.wireOp",EDGE,"E10.sketch_text.stroke-76"),sQuery(id+"F4.wireOp",EDGE,"E10.sketch_text.stroke-77"),sQuery(id+"F4.wireOp",EDGE,"E10.sketch_text.stroke-78"),sQuery(id+"F4.wireOp",EDGE,"E10.sketch_text.stroke-79"),sQuery(id+"F4.wireOp",EDGE,"E10.sketch_text.stroke-80"),sQuery(id+"F4.wireOp",EDGE,"E10.sketch_text.stroke-81"),sQuery(id+"F4.wireOp",EDGE,"E10.sketch_text.stroke-82"),sQuery(id+"F4.wireOp",EDGE,"E10.sketch_text.stroke-83"),sQuery(id+"F4.wireOp",EDGE,"E10.sketch_text.stroke-84"),sQuery(id+"F4.wireOp",EDGE,"E10.sketch_text.stroke-85"),sQuery(id+"F4.wireOp",EDGE,"E10.sketch_text.stroke-86"),sQuery(id+"F4.wireOp",EDGE,"E10.sketch_text.stroke-87"),sQuery(id+"F4.wireOp",EDGE,"E10.sketch_text.stroke-88"),sQuery(id+"F4.wireOp",EDGE,"E10.sketch_text.stroke-89"),sQuery(id+"F4.wireOp",EDGE,"E10.sketch_text.stroke-90"),sQuery(id+"F4.wireOp",EDGE,"E10.sketch_text.stroke-91"),sQuery(id+"F4.wireOp",EDGE,"E10.sketch_text.stroke-92"),sQuery(id+"F4.wireOp",EDGE,"E10.sketch_text.stroke-93"),sQuery(id+"F4.wireOp",EDGE,"E10.sketch_text.stroke-94"),sQuery(id+"F4.wireOp",EDGE,"E10.sketch_text.stroke-95"),sQuery(id+"F4.wireOp",EDGE,"E10.sketch_text.stroke-96"),sQuery(id+"F4.wireOp",EDGE,"E10.sketch_text.stroke-97"),sQuery(id+"F4.wireOp",EDGE,"E10.sketch_text.stroke-98"),sQuery(id+"F4.wireOp",EDGE,"E10.sketch_text.stroke-99"),sQuery(id+"F4.wireOp",EDGE,"E10.sketch_text.stroke-100"),sQuery(id+"F4.wireOp",EDGE,"E10.sketch_text.stroke-101"),sQuery(id+"F4.wireOp",EDGE,"E10.sketch_text.stroke-102"),sQuery(id+"F4.wireOp",EDGE,"E10.sketch_text.stroke-103"),sQuery(id+"F4.wireOp",EDGE,"E10.sketch_text.stroke-104")])],"isStart":false});
            var Q117;
            Q117=makeQuery(id+"F5.opExtrude","SWEPT_FACE",FACE,{"disambiguationData":[OSD([sQuery(id+"F4.wireOp",EDGE,"E10.sketch_text.stroke-33")])]});
            var Q118;
            Q118=makeQuery(id+"F5.opExtrude","SWEPT_FACE",FACE,{"disambiguationData":[OSD([sQuery(id+"F4.wireOp",EDGE,"E10.sketch_text.stroke-93")])]});
            var Q119;
            Q119=makeQuery(id+"F5.opExtrude","SWEPT_FACE",FACE,{"disambiguationData":[OSD([sQuery(id+"F4.wireOp",EDGE,"E10.sketch_text.stroke-34")])]});
            var Q120;
            Q120=makeQuery(id+"F5.opExtrude","SWEPT_FACE",FACE,{"disambiguationData":[OSD([sQuery(id+"F4.wireOp",EDGE,"E10.sketch_text.stroke-152")])]});
            var Q121;
            Q121=makeQuery(id+"F5.opExtrude","SWEPT_FACE",FACE,{"disambiguationData":[OSD([sQuery(id+"F4.wireOp",EDGE,"E10.sketch_text.stroke-51")])]});
            var Q122;
            Q122=makeQuery(id+"F5.opExtrude","SWEPT_FACE",FACE,{"disambiguationData":[OSD([sQuery(id+"F4.wireOp",EDGE,"E10.sketch_text.stroke-6")])]});
            var Q123;
            Q123=makeQuery(id+"F5.opExtrude","SWEPT_FACE",FACE,{"disambiguationData":[OSD([sQuery(id+"F4.wireOp",EDGE,"E10.sketch_text.stroke-7")])]});
            var Q124;
            Q124=makeQuery(id+"F5.opExtrude","SWEPT_FACE",FACE,{"disambiguationData":[OSD([sQuery(id+"F4.wireOp",EDGE,"E10.sketch_text.stroke-156")])]});
            var Q125;
            Q125=makeQuery(id+"F5.opExtrude","SWEPT_FACE",FACE,{"disambiguationData":[OSD([sQuery(id+"F4.wireOp",EDGE,"E10.sketch_text.stroke-112")])]});
            var Q126;
            Q126=makeQuery(id+"F5.boolean.opBoolean","SPLIT",FACE,{"disambiguationData":[TD([makeQuery(id+"F5.opExtrude","SWEPT_FACE",FACE,{"disambiguationData":[OSD([sQuery(id+"F4.wireOp",EDGE,"E10.sketch_text.stroke-182")])]})])],"derivedFrom":makeQuery(id+"F1.opExtrude","CAP_FACE",FACE,{"disambiguationData":[OSD([sQuery(id+"F0.wireOp",EDGE,"E0.bottom"),sQuery(id+"F0.wireOp",EDGE,"E0.top"),sQuery(id+"F0.wireOp",EDGE,"E0.left"),sQuery(id+"F0.wireOp",EDGE,"E0.right"),sQuery(id+"F0.wireOp",EDGE,"E1"),sQuery(id+"F0.wireOp",EDGE,"E7.MirrorC"),sQuery(id+"F0.wireOp",EDGE,"E8.MirrorC"),sQuery(id+"F0.wireOp",EDGE,"E9.MirrorC")])],"isStart":true})});
            var Q127;
            Q127=makeQuery(id+"F5.opExtrude","SWEPT_FACE",FACE,{"disambiguationData":[OSD([sQuery(id+"F4.wireOp",EDGE,"E10.sketch_text.stroke-96")])]});
            var Q128;
            Q128=makeQuery(id+"F5.opExtrude","SWEPT_FACE",FACE,{"disambiguationData":[OSD([sQuery(id+"F4.wireOp",EDGE,"E10.sketch_text.stroke-114")])]});
            var Q129;
            Q129=makeQuery(id+"F5.opExtrude","SWEPT_FACE",FACE,{"disambiguationData":[OSD([sQuery(id+"F4.wireOp",EDGE,"E10.sketch_text.stroke-39")])]});
            var Q130;
            Q130=makeQuery(id+"F5.opExtrude","SWEPT_FACE",FACE,{"disambiguationData":[OSD([sQuery(id+"F4.wireOp",EDGE,"E10.sketch_text.stroke-13")])]});
            var Q131;
            Q131=makeQuery(id+"F5.opExtrude","SWEPT_FACE",FACE,{"disambiguationData":[OSD([sQuery(id+"F4.wireOp",EDGE,"E10.sketch_text.stroke-115")])]});
            var Q132;
            Q132=makeQuery(id+"F5.opExtrude","SWEPT_FACE",FACE,{"disambiguationData":[OSD([sQuery(id+"F4.wireOp",EDGE,"E10.sketch_text.stroke-56")])]});
            var Q133;
            Q133=makeQuery(id+"F5.opExtrude","SWEPT_FACE",FACE,{"disambiguationData":[OSD([sQuery(id+"F4.wireOp",EDGE,"E10.sketch_text.stroke-144")])]});
            var Q134;
            Q134=makeQuery(id+"F5.opExtrude","SWEPT_FACE",FACE,{"disambiguationData":[OSD([sQuery(id+"F4.wireOp",EDGE,"E10.sketch_text.stroke-190")])]});
            var Q135;
            Q135=makeQuery(id+"F5.opExtrude","SWEPT_FACE",FACE,{"disambiguationData":[OSD([sQuery(id+"F4.wireOp",EDGE,"E10.sketch_text.stroke-116")])]});
            var Q136;
            Q136=makeQuery(id+"F5.opExtrude","SWEPT_FACE",FACE,{"disambiguationData":[OSD([sQuery(id+"F4.wireOp",EDGE,"E10.sketch_text.stroke-41")])]});
            var Q137;
            Q137=makeQuery(id+"F5.opExtrude","SWEPT_FACE",FACE,{"disambiguationData":[OSD([sQuery(id+"F4.wireOp",EDGE,"E10.sketch_text.stroke-161")])]});
            var Q138;
            Q138=makeQuery(id+"F5.opExtrude","SWEPT_FACE",FACE,{"disambiguationData":[OSD([sQuery(id+"F4.wireOp",EDGE,"E10.sketch_text.stroke-146")])]});
            var Q139;
            Q139=makeQuery(id+"F5.opExtrude","SWEPT_FACE",FACE,{"disambiguationData":[OSD([sQuery(id+"F4.wireOp",EDGE,"E10.sketch_text.stroke-58")])]});
            var Q140;
            Q140=makeQuery(id+"F5.opExtrude","SWEPT_FACE",FACE,{"disambiguationData":[OSD([sQuery(id+"F4.wireOp",EDGE,"E10.sketch_text.stroke-105")])]});
            var Q141;
            Q141=makeQuery(id+"F5.opExtrude","SWEPT_FACE",FACE,{"disambiguationData":[OSD([sQuery(id+"F4.wireOp",EDGE,"E10.sketch_text.stroke-177")])]});
            var Q142;
            Q142=makeQuery(id+"F5.opExtrude","SWEPT_FACE",FACE,{"disambiguationData":[OSD([sQuery(id+"F4.wireOp",EDGE,"E10.sketch_text.stroke-77")])]});
            var Q143;
            Q143=makeQuery(id+"F5.opExtrude","SWEPT_FACE",FACE,{"disambiguationData":[OSD([sQuery(id+"F4.wireOp",EDGE,"E10.sketch_text.stroke-138")])]});
            var Q144;
            Q144=makeQuery(id+"F5.opExtrude","SWEPT_FACE",FACE,{"disambiguationData":[OSD([sQuery(id+"F4.wireOp",EDGE,"E10.sketch_text.stroke-111")])]});
            var Q145;
            Q145=makeQuery(id+"F5.opExtrude","SWEPT_FACE",FACE,{"disambiguationData":[OSD([sQuery(id+"F4.wireOp",EDGE,"E10.sketch_text.stroke-53")])]});
            var Q146;
            Q146=makeQuery(id+"F5.opExtrude","SWEPT_FACE",FACE,{"disambiguationData":[OSD([sQuery(id+"F4.wireOp",EDGE,"E10.sketch_text.stroke-141")])]});
            var Q147;
            Q147=makeQuery(id+"F5.opExtrude","SWEPT_FACE",FACE,{"disambiguationData":[OSD([sQuery(id+"F4.wireOp",EDGE,"E10.sketch_text.stroke-157")])]});
            var Q148;
            Q148=makeQuery(id+"F5.opExtrude","SWEPT_FACE",FACE,{"disambiguationData":[OSD([sQuery(id+"F4.wireOp",EDGE,"E10.sketch_text.stroke-64")])]});
            var Q149;
            Q149=makeQuery(id+"F5.boolean.opBoolean","SPLIT",FACE,{"disambiguationData":[TD([makeQuery(id+"F5.opExtrude","SWEPT_FACE",FACE,{"disambiguationData":[OSD([sQuery(id+"F4.wireOp",EDGE,"E10.sketch_text.stroke-53")])]})])],"derivedFrom":makeQuery(id+"F1.opExtrude","CAP_FACE",FACE,{"disambiguationData":[OSD([sQuery(id+"F0.wireOp",EDGE,"E0.bottom"),sQuery(id+"F0.wireOp",EDGE,"E0.top"),sQuery(id+"F0.wireOp",EDGE,"E0.left"),sQuery(id+"F0.wireOp",EDGE,"E0.right"),sQuery(id+"F0.wireOp",EDGE,"E1"),sQuery(id+"F0.wireOp",EDGE,"E7.MirrorC"),sQuery(id+"F0.wireOp",EDGE,"E8.MirrorC"),sQuery(id+"F0.wireOp",EDGE,"E9.MirrorC")])],"isStart":true})});
            var Q150;
            Q150=makeQuery(id+"F5.opExtrude","SWEPT_FACE",FACE,{"disambiguationData":[OSD([sQuery(id+"F4.wireOp",EDGE,"E10.sketch_text.stroke-36")])]});
            var Q151;
            Q151=makeQuery(id+"F5.opExtrude","SWEPT_FACE",FACE,{"disambiguationData":[OSD([sQuery(id+"F4.wireOp",EDGE,"E10.sketch_text.stroke-22")])]});
            var Q152;
            Q152=makeQuery(id+"F5.boolean.opBoolean","SPLIT",FACE,{"disambiguationData":[TD([makeQuery(id+"F5.opExtrude","SWEPT_FACE",FACE,{"disambiguationData":[OSD([sQuery(id+"F4.wireOp",EDGE,"E10.sketch_text.stroke-119")])]})])],"derivedFrom":makeQuery(id+"F1.opExtrude","CAP_FACE",FACE,{"disambiguationData":[OSD([sQuery(id+"F0.wireOp",EDGE,"E0.bottom"),sQuery(id+"F0.wireOp",EDGE,"E0.top"),sQuery(id+"F0.wireOp",EDGE,"E0.left"),sQuery(id+"F0.wireOp",EDGE,"E0.right"),sQuery(id+"F0.wireOp",EDGE,"E1"),sQuery(id+"F0.wireOp",EDGE,"E7.MirrorC"),sQuery(id+"F0.wireOp",EDGE,"E8.MirrorC"),sQuery(id+"F0.wireOp",EDGE,"E9.MirrorC")])],"isStart":true})});
            var Q153;
            Q153=makeQuery(id+"F5.boolean.opBoolean","SPLIT",FACE,{"disambiguationData":[TD([makeQuery(id+"F5.opExtrude","SWEPT_FACE",FACE,{"disambiguationData":[OSD([sQuery(id+"F4.wireOp",EDGE,"E10.sketch_text.stroke-158")])]})])],"derivedFrom":makeQuery(id+"F1.opExtrude","CAP_FACE",FACE,{"disambiguationData":[OSD([sQuery(id+"F0.wireOp",EDGE,"E0.bottom"),sQuery(id+"F0.wireOp",EDGE,"E0.top"),sQuery(id+"F0.wireOp",EDGE,"E0.left"),sQuery(id+"F0.wireOp",EDGE,"E0.right"),sQuery(id+"F0.wireOp",EDGE,"E1"),sQuery(id+"F0.wireOp",EDGE,"E7.MirrorC"),sQuery(id+"F0.wireOp",EDGE,"E8.MirrorC"),sQuery(id+"F0.wireOp",EDGE,"E9.MirrorC")])],"isStart":true})});
            var Q154;
            Q154=makeQuery(id+"F5.opExtrude","SWEPT_FACE",FACE,{"disambiguationData":[OSD([sQuery(id+"F4.wireOp",EDGE,"E10.sketch_text.stroke-9")])]});
            var Q155;
            Q155=makeQuery(id+"F5.opExtrude","SWEPT_FACE",FACE,{"disambiguationData":[OSD([sQuery(id+"F4.wireOp",EDGE,"E10.sketch_text.stroke-167")])]});
            var Q156;
            Q156=makeQuery(id+"F5.opExtrude","SWEPT_FACE",FACE,{"disambiguationData":[OSD([sQuery(id+"F4.wireOp",EDGE,"E10.sketch_text.stroke-95")])]});
            var Q157;
            Q157=makeQuery(id+"F5.opExtrude","SWEPT_FACE",FACE,{"disambiguationData":[OSD([sQuery(id+"F4.wireOp",EDGE,"E10.sketch_text.stroke-184")])]});
            var Q158;
            Q158=makeQuery(id+"F5.opExtrude","SWEPT_FACE",FACE,{"disambiguationData":[OSD([sQuery(id+"F4.wireOp",EDGE,"E10.sketch_text.stroke-84")])]});
            var Q159;
            Q159=makeQuery(id+"F5.opExtrude","SWEPT_FACE",FACE,{"disambiguationData":[OSD([sQuery(id+"F4.wireOp",EDGE,"E10.sketch_text.stroke-68")])]});
            var Q160;
            Q160=makeQuery(id+"F5.opExtrude","SWEPT_FACE",FACE,{"disambiguationData":[OSD([sQuery(id+"F4.wireOp",EDGE,"E10.sketch_text.stroke-143")])]});
            var Q161;
            Q161=makeQuery(id+"F5.opExtrude","SWEPT_FACE",FACE,{"disambiguationData":[OSD([sQuery(id+"F4.wireOp",EDGE,"E10.sketch_text.stroke-189")])]});
            var Q162;
            Q162=makeQuery(id+"F5.opExtrude","CAP_FACE",FACE,{"disambiguationData":[OSD([sQuery(id+"F4.wireOp",EDGE,"E10.sketch_text.stroke-13"),sQuery(id+"F4.wireOp",EDGE,"E10.sketch_text.stroke-14"),sQuery(id+"F4.wireOp",EDGE,"E10.sketch_text.stroke-15"),sQuery(id+"F4.wireOp",EDGE,"E10.sketch_text.stroke-16"),sQuery(id+"F4.wireOp",EDGE,"E10.sketch_text.stroke-17"),sQuery(id+"F4.wireOp",EDGE,"E10.sketch_text.stroke-18"),sQuery(id+"F4.wireOp",EDGE,"E10.sketch_text.stroke-19"),sQuery(id+"F4.wireOp",EDGE,"E10.sketch_text.stroke-20")])],"isStart":false});
            var Q163;
            Q163=makeQuery(id+"F5.opExtrude","SWEPT_FACE",FACE,{"disambiguationData":[OSD([sQuery(id+"F4.wireOp",EDGE,"E10.sketch_text.stroke-57")])]});
            var Q164;
            Q164=makeQuery(id+"F5.opExtrude","SWEPT_FACE",FACE,{"disambiguationData":[OSD([sQuery(id+"F4.wireOp",EDGE,"E10.sketch_text.stroke-29")])]});
            var Q165;
            Q165=makeQuery(id+"F5.opExtrude","SWEPT_FACE",FACE,{"disambiguationData":[OSD([sQuery(id+"F4.wireOp",EDGE,"E10.sketch_text.stroke-60")])]});
            var Q166;
            Q166=makeQuery(id+"F5.opExtrude","SWEPT_FACE",FACE,{"disambiguationData":[OSD([sQuery(id+"F4.wireOp",EDGE,"E10.sketch_text.stroke-148")])]});
            var Q167;
            Q167=makeQuery(id+"F5.opExtrude","SWEPT_FACE",FACE,{"disambiguationData":[OSD([sQuery(id+"F4.wireOp",EDGE,"E10.sketch_text.stroke-75")])]});
            var Q168;
            Q168=makeQuery(id+"F5.opExtrude","SWEPT_FACE",FACE,{"disambiguationData":[OSD([sQuery(id+"F4.wireOp",EDGE,"E10.sketch_text.stroke-91")])]});
            var Q169;
            Q169=makeQuery(id+"F5.opExtrude","SWEPT_FACE",FACE,{"disambiguationData":[OSD([sQuery(id+"F4.wireOp",EDGE,"E10.sketch_text.stroke-78")])]});
            var Q170;
            Q170=makeQuery(id+"F5.opExtrude","SWEPT_FACE",FACE,{"disambiguationData":[OSD([sQuery(id+"F4.wireOp",EDGE,"E10.sketch_text.stroke-62")])]});
            var Q171;
            Q171=makeQuery(id+"F5.opExtrude","SWEPT_FACE",FACE,{"disambiguationData":[OSD([sQuery(id+"F4.wireOp",EDGE,"E10.sketch_text.stroke-182")])]});
            var Q172;
            Q172=makeQuery(id+"F5.opExtrude","SWEPT_FACE",FACE,{"disambiguationData":[OSD([sQuery(id+"F4.wireOp",EDGE,"E10.sketch_text.stroke-11")])]});
            var Q173;
            Q173=makeQuery(id+"F5.opExtrude","SWEPT_FACE",FACE,{"disambiguationData":[OSD([sQuery(id+"F4.wireOp",EDGE,"E10.sketch_text.stroke-97")])]});
            var Q174;
            Q174=makeQuery(id+"F5.opExtrude","SWEPT_FACE",FACE,{"disambiguationData":[OSD([sQuery(id+"F4.wireOp",EDGE,"E10.sketch_text.stroke-23")])]});
            var Q175;
            Q175=makeQuery(id+"F5.opExtrude","SWEPT_FACE",FACE,{"disambiguationData":[OSD([sQuery(id+"F4.wireOp",EDGE,"E10.sketch_text.stroke-80")])]});
            var Q176;
            Q176=makeQuery(id+"F5.boolean.opBoolean","SPLIT",FACE,{"disambiguationData":[TD([makeQuery(id+"F5.opExtrude","SWEPT_FACE",FACE,{"disambiguationData":[OSD([sQuery(id+"F4.wireOp",EDGE,"E10.sketch_text.stroke-99")])]})])],"derivedFrom":makeQuery(id+"F1.opExtrude","CAP_FACE",FACE,{"disambiguationData":[OSD([sQuery(id+"F0.wireOp",EDGE,"E0.bottom"),sQuery(id+"F0.wireOp",EDGE,"E0.top"),sQuery(id+"F0.wireOp",EDGE,"E0.left"),sQuery(id+"F0.wireOp",EDGE,"E0.right"),sQuery(id+"F0.wireOp",EDGE,"E1"),sQuery(id+"F0.wireOp",EDGE,"E7.MirrorC"),sQuery(id+"F0.wireOp",EDGE,"E8.MirrorC"),sQuery(id+"F0.wireOp",EDGE,"E9.MirrorC")])],"isStart":true})});
            var Q177;
            Q177=makeQuery(id+"F5.opExtrude","SWEPT_FACE",FACE,{"disambiguationData":[OSD([sQuery(id+"F4.wireOp",EDGE,"E10.sketch_text.stroke-168")])]});
            var Q178;
            Q178=makeQuery(id+"F5.opExtrude","SWEPT_FACE",FACE,{"disambiguationData":[OSD([sQuery(id+"F4.wireOp",EDGE,"E10.sketch_text.stroke-188")])]});
            var Q179;
            Q179=makeQuery(id+"F5.opExtrude","SWEPT_FACE",FACE,{"disambiguationData":[OSD([sQuery(id+"F4.wireOp",EDGE,"E10.sketch_text.stroke-129")])]});
            var Q180;
            Q180=makeQuery(id+"F5.opExtrude","SWEPT_FACE",FACE,{"disambiguationData":[OSD([sQuery(id+"F4.wireOp",EDGE,"E10.sketch_text.stroke-27")])]});
            var Q181;
            Q181=makeQuery(id+"F5.opExtrude","SWEPT_FACE",FACE,{"disambiguationData":[OSD([sQuery(id+"F4.wireOp",EDGE,"E10.sketch_text.stroke-175")])]});
            var Q182;
            Q182=makeQuery(id+"F5.opExtrude","SWEPT_FACE",FACE,{"disambiguationData":[OSD([sQuery(id+"F4.wireOp",EDGE,"E10.sketch_text.stroke-42")])]});
            var Q183;
            Q183=makeQuery(id+"F5.opExtrude","SWEPT_FACE",FACE,{"disambiguationData":[OSD([sQuery(id+"F4.wireOp",EDGE,"E10.sketch_text.stroke-118")])]});
            var Q184;
            Q184=makeQuery(id+"F5.opExtrude","SWEPT_FACE",FACE,{"disambiguationData":[OSD([sQuery(id+"F4.wireOp",EDGE,"E10.sketch_text.stroke-151")])]});
            var Q185;
            Q185=makeQuery(id+"F5.opExtrude","SWEPT_FACE",FACE,{"disambiguationData":[OSD([sQuery(id+"F4.wireOp",EDGE,"E10.sketch_text.stroke-137")])]});
            var Q186;
            Q186=makeQuery(id+"F5.opExtrude","SWEPT_FACE",FACE,{"disambiguationData":[OSD([sQuery(id+"F4.wireOp",EDGE,"E10.sketch_text.stroke-83")])]});
            var Q187;
            Q187=makeQuery(id+"F5.boolean.opBoolean","SPLIT",FACE,{"disambiguationData":[TD([makeQuery(id+"F5.opExtrude","SWEPT_FACE",FACE,{"disambiguationData":[OSD([sQuery(id+"F4.wireOp",EDGE,"E10.sketch_text.stroke-90")])]})])],"derivedFrom":makeQuery(id+"F1.opExtrude","CAP_FACE",FACE,{"disambiguationData":[OSD([sQuery(id+"F0.wireOp",EDGE,"E0.bottom"),sQuery(id+"F0.wireOp",EDGE,"E0.top"),sQuery(id+"F0.wireOp",EDGE,"E0.left"),sQuery(id+"F0.wireOp",EDGE,"E0.right"),sQuery(id+"F0.wireOp",EDGE,"E1"),sQuery(id+"F0.wireOp",EDGE,"E7.MirrorC"),sQuery(id+"F0.wireOp",EDGE,"E8.MirrorC"),sQuery(id+"F0.wireOp",EDGE,"E9.MirrorC")])],"isStart":true})});
            var Q188;
            Q188=makeQuery(id+"F5.opExtrude","SWEPT_FACE",FACE,{"disambiguationData":[OSD([sQuery(id+"F4.wireOp",EDGE,"E10.sketch_text.stroke-139")])]});
            var Q189;
            Q189=makeQuery(id+"F5.opExtrude","SWEPT_FACE",FACE,{"disambiguationData":[OSD([sQuery(id+"F4.wireOp",EDGE,"E10.sketch_text.stroke-70")])]});
            var Q190;
            Q190=makeQuery(id+"F5.opExtrude","SWEPT_FACE",FACE,{"disambiguationData":[OSD([sQuery(id+"F4.wireOp",EDGE,"E10.sketch_text.stroke-160")])]});
            var Q191;
            Q191=makeQuery(id+"F5.opExtrude","SWEPT_FACE",FACE,{"disambiguationData":[OSD([sQuery(id+"F4.wireOp",EDGE,"E10.sketch_text.stroke-71")])]});
            var Q192;
            Q192=makeQuery(id+"F5.opExtrude","SWEPT_FACE",FACE,{"disambiguationData":[OSD([sQuery(id+"F4.wireOp",EDGE,"E10.sketch_text.stroke-117")])]});
            var Q193;
            Q193=makeQuery(id+"F5.opExtrude","SWEPT_FACE",FACE,{"disambiguationData":[OSD([sQuery(id+"F4.wireOp",EDGE,"E10.sketch_text.stroke-147")])]});
            var Q194;
            Q194=makeQuery(id+"F5.opExtrude","SWEPT_FACE",FACE,{"disambiguationData":[OSD([sQuery(id+"F4.wireOp",EDGE,"E10.sketch_text.stroke-164")])]});
            var Q195;
            Q195=makeQuery(id+"F5.opExtrude","SWEPT_FACE",FACE,{"disambiguationData":[OSD([sQuery(id+"F4.wireOp",EDGE,"E10.sketch_text.stroke-61")])]});
            var Q196;
            Q196=makeQuery(id+"F5.opExtrude","SWEPT_FACE",FACE,{"disambiguationData":[OSD([sQuery(id+"F4.wireOp",EDGE,"E10.sketch_text.stroke-19")])]});
            var Q197;
            Q197=makeQuery(id+"F5.opExtrude","SWEPT_FACE",FACE,{"disambiguationData":[OSD([sQuery(id+"F4.wireOp",EDGE,"E10.sketch_text.stroke-35")])]});
            var Q198;
            Q198=makeQuery(id+"F5.opExtrude","SWEPT_FACE",FACE,{"disambiguationData":[OSD([sQuery(id+"F4.wireOp",EDGE,"E10.sketch_text.stroke-140")])]});
            var Q199;
            Q199=makeQuery(id+"F5.opExtrude","SWEPT_FACE",FACE,{"disambiguationData":[OSD([sQuery(id+"F4.wireOp",EDGE,"E10.sketch_text.stroke-20")])]});
            var Q200;
            Q200=makeQuery(id+"F5.opExtrude","SWEPT_FACE",FACE,{"disambiguationData":[OSD([sQuery(id+"F4.wireOp",EDGE,"E10.sketch_text.stroke-16")])]});
            var Q201;
            Q201=makeQuery(id+"F5.opExtrude","SWEPT_FACE",FACE,{"disambiguationData":[OSD([sQuery(id+"F4.wireOp",EDGE,"E10.sketch_text.stroke-18")])]});
            var Q202;
            Q202=makeQuery(id+"F5.opExtrude","SWEPT_FACE",FACE,{"disambiguationData":[OSD([sQuery(id+"F4.wireOp",EDGE,"E10.sketch_text.stroke-17")])]});
            var Q203;
            Q203=qCreatedBy(makeId("Right.planeOp"),FACE);
            mirror(context, id + "F6", {"operationType" : NewBodyOperationType.ADD, "entities" : qUnion([Q0]), "faces" : qUnion([Q1, Q2, Q3, Q4, Q5, Q6, Q7, Q8, Q9, Q10, Q11, Q12, Q13, Q14, Q15, Q16, Q17, Q18, Q19, Q20, Q21, Q22, Q23, Q24, Q25, Q26, Q27, Q28, Q29, Q30, Q31, Q32, Q33, Q34, Q35, Q36, Q37, Q38, Q39, Q40, Q41, Q42, Q43, Q44, Q45, Q46, Q47, Q48, Q49, Q50, Q51, Q52, Q53, Q54, Q55, Q56, Q57, Q58, Q59, Q60, Q61, Q62, Q63, Q64, Q65, Q66, Q67, Q68, Q69, Q70, Q71, Q72, Q73, Q74, Q75, Q76, Q77, Q78, Q79, Q80, Q81, Q82, Q83, Q84, Q85, Q86, Q87, Q88, Q89, Q90, Q91, Q92, Q93, Q94, Q95, Q96, Q97, Q98, Q99, Q100, Q101, Q102, Q103, Q104, Q105, Q106, Q107, Q108, Q109, Q110, Q111, Q112, Q113, Q114, Q115, Q116, Q117, Q118, Q119, Q120, Q121, Q122, Q123, Q124, Q125, Q126, Q127, Q128, Q129, Q130, Q131, Q132, Q133, Q134, Q135, Q136, Q137, Q138, Q139, Q140, Q141, Q142, Q143, Q144, Q145, Q146, Q147, Q148, Q149, Q150, Q151, Q152, Q153, Q154, Q155, Q156, Q157, Q158, Q159, Q160, Q161, Q162, Q163, Q164, Q165, Q166, Q167, Q168, Q169, Q170, Q171, Q172, Q173, Q174, Q175, Q176, Q177, Q178, Q179, Q180, Q181, Q182, Q183, Q184, Q185, Q186, Q187, Q188, Q189, Q190, Q191, Q192, Q193, Q194, Q195, Q196, Q197, Q198, Q199, Q200, Q201, Q202]), "mirrorPlane" : qUnion([Q203])});
        }
    });
